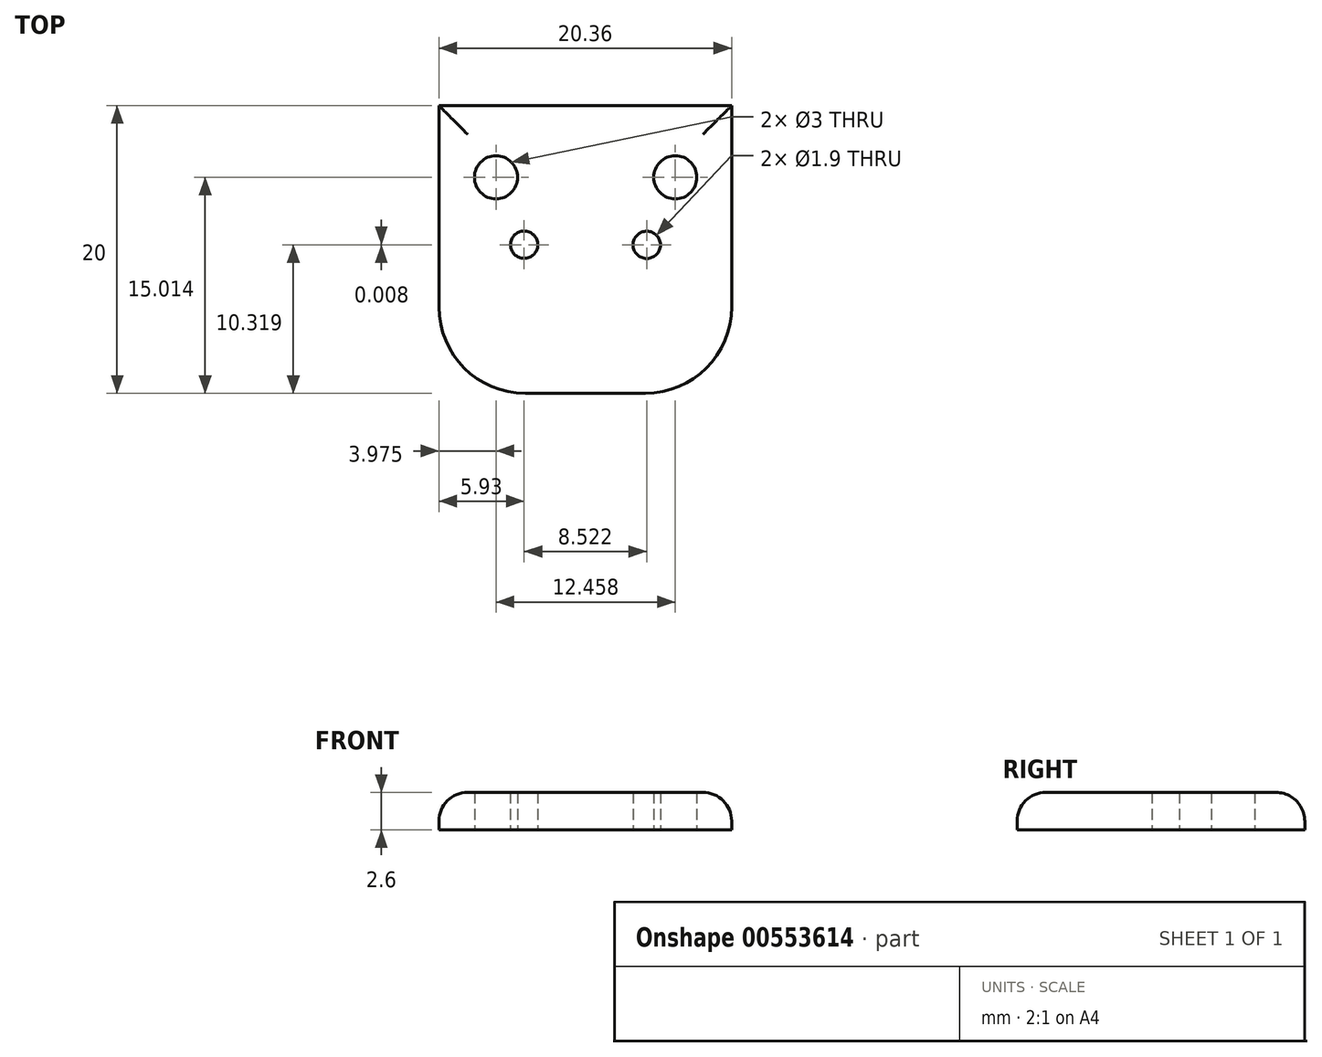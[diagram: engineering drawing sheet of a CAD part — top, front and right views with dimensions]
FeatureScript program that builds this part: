
annotation { "Feature Type Name" : "Feature", "Feature Type Description" : "" }
export const myFeature = defineFeature(function(context is Context, id is Id, definition is map)
    precondition{}
    {
        {
            var Q0;
            Q0=qCreatedBy(makeId("Top.planeOp"),FACE);
            var sketch = newSketch(context, id + "F0", { "sketchPlane" : qUnion([Q0])});
            skLineSegment(sketch, "E0.bottom", {"start": v(-10.18, -10) * mm, "end": v(10.18, -10) * mm});
            skLineSegment(sketch, "E0.top", {"start": v(-10.18, 10) * mm, "end": v(10.18, 10) * mm});
            skLineSegment(sketch, "E0.left", {"start": v(-10.18, -10) * mm, "end": v(-10.18, 10) * mm});
            skLineSegment(sketch, "E0.right", {"start": v(10.18, -10) * mm, "end": v(10.18, 10) * mm});
            skPoint(sketch, "E0.middle", {"position": v(0, 0) * mm});
            skSolve(sketch);
        }
        {
            var Q0;
            Q0 = qSketchRegion(id + "F0", true);
            extrude(context, id + "F1", {"entities" : qUnion([Q0]), "depth" : 2.6 * mm, "offsetDistance" : 25 * mm});
        }
        {
            var Q0;
            Q0=qCreatedBy(makeId("Top.planeOp"),FACE);
            var sketch = newSketch(context, id + "F2", { "sketchPlane" : qUnion([Q0])});
            skCircle(sketch, "E1", {"center": v(-6.2, 5.01) * mm, "radius": 1.5 * mm});
            skCircle(sketch, "E2", {"center": v(6.25, 5.01) * mm, "radius": 1.5 * mm});
            skSolve(sketch);
        }
        {
            var Q0;
            Q0 = qSketchRegion(id + "F2", true);
            extrude(context, id + "F3", {"entities" : qUnion([Q0]), "operationType" : NewBodyOperationType.REMOVE, "depth" : 25 * mm, "offsetDistance" : 25 * mm});
        }
        {
            var Q0;
            Q0=qCreatedBy(makeId("Top.planeOp"),FACE);
            var sketch = newSketch(context, id + "F4", { "sketchPlane" : qUnion([Q0])});
            skCircle(sketch, "E3", {"center": v(-4.25, 0.33) * mm, "radius": 0.95 * mm});
            skCircle(sketch, "E4", {"center": v(4.27, 0.32) * mm, "radius": 0.95 * mm});
            skSolve(sketch);
        }
        {
            var Q0;
            Q0 = qSketchRegion(id + "F4", true);
            extrude(context, id + "F5", {"entities" : qUnion([Q0]), "operationType" : NewBodyOperationType.REMOVE, "depth" : 25 * mm, "offsetDistance" : 25 * mm});
        }
        {
            var Q0;
            Q0=makeQuery(id+"F1.opExtrude","SWEPT_EDGE",EDGE,{"disambiguationData":[OSD([sQuery(id+"F0.wireOp",EDGE,"E0.bottom"),sQuery(id+"F0.wireOp",EDGE,"E0.right")])]});
            var Q1;
            Q1=makeQuery(id+"F1.opExtrude","SWEPT_EDGE",EDGE,{"disambiguationData":[OSD([sQuery(id+"F0.wireOp",EDGE,"E0.bottom"),sQuery(id+"F0.wireOp",EDGE,"E0.left")])]});
            fillet(context, id + "F6", {"entities" : qUnion([Q0, Q1]), "radius" : 6 * mm, "tangentPropagation" : true, "allowEdgeOverflow" : false});
        }
        {
            var Q0;
            {var subQ0=sQuery(id+"F0.wireOp",EDGE,"E0.left");var subQ1=sQuery(id+"F0.wireOp",EDGE,"E0.bottom");Q0=makeQuery(id+"F6.opFillet","BLEND_EDGE",EDGE,{"blendedFrom":[makeQuery(id+"F1.opExtrude","SWEPT_EDGE",EDGE,{"disambiguationData":[OSD([subQ1,subQ0])]}),makeQuery(id+"F1.opExtrude","CAP_FACE",FACE,{"disambiguationData":[OSD([subQ1,sQuery(id+"F0.wireOp",EDGE,"E0.top"),subQ0,sQuery(id+"F0.wireOp",EDGE,"E0.right")])],"isStart":false})],"blendedInto":[makeQuery(id+"F1.opExtrude","CAP_FACE",FACE,{"disambiguationData":[OSD([subQ1,sQuery(id+"F0.wireOp",EDGE,"E0.top"),subQ0,sQuery(id+"F0.wireOp",EDGE,"E0.right")])],"isStart":false})]});}
            var Q1;
            {var subQ0=sQuery(id+"F0.wireOp",EDGE,"E0.right");var subQ1=sQuery(id+"F0.wireOp",EDGE,"E0.bottom");Q1=makeQuery(id+"F6.opFillet","BLEND_EDGE",EDGE,{"blendedFrom":[makeQuery(id+"F1.opExtrude","SWEPT_EDGE",EDGE,{"disambiguationData":[OSD([subQ1,subQ0])]}),makeQuery(id+"F1.opExtrude","CAP_FACE",FACE,{"disambiguationData":[OSD([subQ1,sQuery(id+"F0.wireOp",EDGE,"E0.top"),sQuery(id+"F0.wireOp",EDGE,"E0.left"),subQ0])],"isStart":false})],"blendedInto":[makeQuery(id+"F1.opExtrude","CAP_FACE",FACE,{"disambiguationData":[OSD([subQ1,sQuery(id+"F0.wireOp",EDGE,"E0.top"),sQuery(id+"F0.wireOp",EDGE,"E0.left"),subQ0])],"isStart":false})]});}
            var Q2;
            Q2=makeQuery(id+"F1.opExtrude","CAP_EDGE",EDGE,{"disambiguationData":[OSD([sQuery(id+"F0.wireOp",EDGE,"E0.right")])],"isStart":false});
            var Q3;
            Q3=makeQuery(id+"F1.opExtrude","CAP_EDGE",EDGE,{"disambiguationData":[OSD([sQuery(id+"F0.wireOp",EDGE,"E0.top")])],"isStart":false});
            var Q4;
            Q4=makeQuery(id+"F1.opExtrude","CAP_EDGE",EDGE,{"disambiguationData":[OSD([sQuery(id+"F0.wireOp",EDGE,"E0.left")])],"isStart":false});
            var Q5;
            Q5=makeQuery(id+"F1.opExtrude","CAP_EDGE",EDGE,{"disambiguationData":[OSD([sQuery(id+"F0.wireOp",EDGE,"E0.bottom")])],"isStart":false});
            fillet(context, id + "F7", {"entities" : qUnion([Q0, Q1, Q2, Q3, Q4, Q5]), "radius" : 2 * mm, "tangentPropagation" : true, "allowEdgeOverflow" : false});
        }
    });
